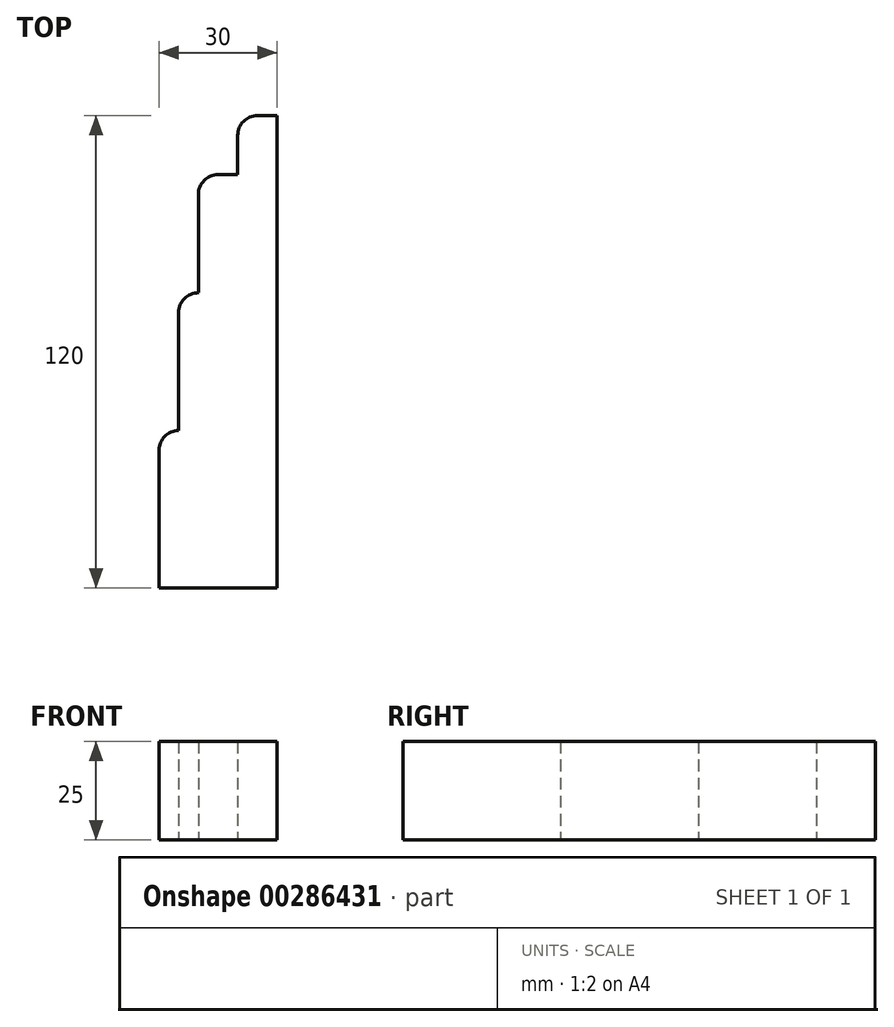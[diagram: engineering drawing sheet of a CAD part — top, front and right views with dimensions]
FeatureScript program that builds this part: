
annotation { "Feature Type Name" : "Feature", "Feature Type Description" : "" }
export const myFeature = defineFeature(function(context is Context, id is Id, definition is map)
    precondition{}
    {
        {
            var Q0;
            Q0=qCreatedBy(makeId("Top.planeOp"),FACE);
            var sketch = newSketch(context, id + "F0", { "sketchPlane" : qUnion([Q0])});
            skLineSegment(sketch, "E0", {"start": v(-28.6, -62.94) * mm, "end": v(1.4, -62.94) * mm});
            skLineSegment(sketch, "E1", {"start": v(1.4, -62.94) * mm, "end": v(1.4, 57.06) * mm});
            skLineSegment(sketch, "E2", {"start": v(1.4, 57.06) * mm, "end": v(-3.6, 57.06) * mm});
            skLineSegment(sketch, "E3", {"start": v(-8.6, 52.06) * mm, "end": v(-8.6, 42.06) * mm});
            skLineSegment(sketch, "E4", {"start": v(-8.6, 42.06) * mm, "end": v(-13.6, 42.06) * mm});
            skLineSegment(sketch, "E5", {"start": v(-18.6, 37.06) * mm, "end": v(-18.6, 12.06) * mm});
            skLineSegment(sketch, "E6", {"start": v(-18.6, 12.06) * mm, "end": v(-18.6, 12.06) * mm});
            skLineSegment(sketch, "E7", {"start": v(-23.6, 7.06) * mm, "end": v(-23.6, -22.94) * mm});
            skLineSegment(sketch, "E8", {"start": v(-23.6, -22.94) * mm, "end": v(-23.6, -22.94) * mm});
            skLineSegment(sketch, "E9", {"start": v(-28.6, -27.94) * mm, "end": v(-28.6, -62.94) * mm});
            skPoint(sketch, "E10.visualSharp", {"position": v(-28.6, -22.94) * mm});
            skArc(sketch, "E10.filletArc", {"start": v(-23.6, -22.94) * mm, "mid": v(-27.14, -24.4) * mm, "end": v(-28.6, -27.94) * mm});
            skPoint(sketch, "E11.visualSharp", {"position": v(-23.6, 12.06) * mm});
            skArc(sketch, "E11.filletArc", {"start": v(-18.6, 12.06) * mm, "mid": v(-22.14, 10.6) * mm, "end": v(-23.6, 7.06) * mm});
            skPoint(sketch, "E12.visualSharp", {"position": v(-18.6, 42.06) * mm});
            skArc(sketch, "E12.filletArc", {"start": v(-13.6, 42.06) * mm, "mid": v(-17.14, 40.6) * mm, "end": v(-18.6, 37.06) * mm});
            skPoint(sketch, "E13.visualSharp", {"position": v(-8.6, 57.06) * mm});
            skArc(sketch, "E13.filletArc", {"start": v(-3.6, 57.06) * mm, "mid": v(-7.14, 55.6) * mm, "end": v(-8.6, 52.06) * mm});
            skSolve(sketch);
        }
        {
            var Q0;
            Q0 = qSketchRegion(id + "F0", true);
            extrude(context, id + "F1", {"entities" : qUnion([Q0]), "depth" : 25 * mm});
        }
    });
